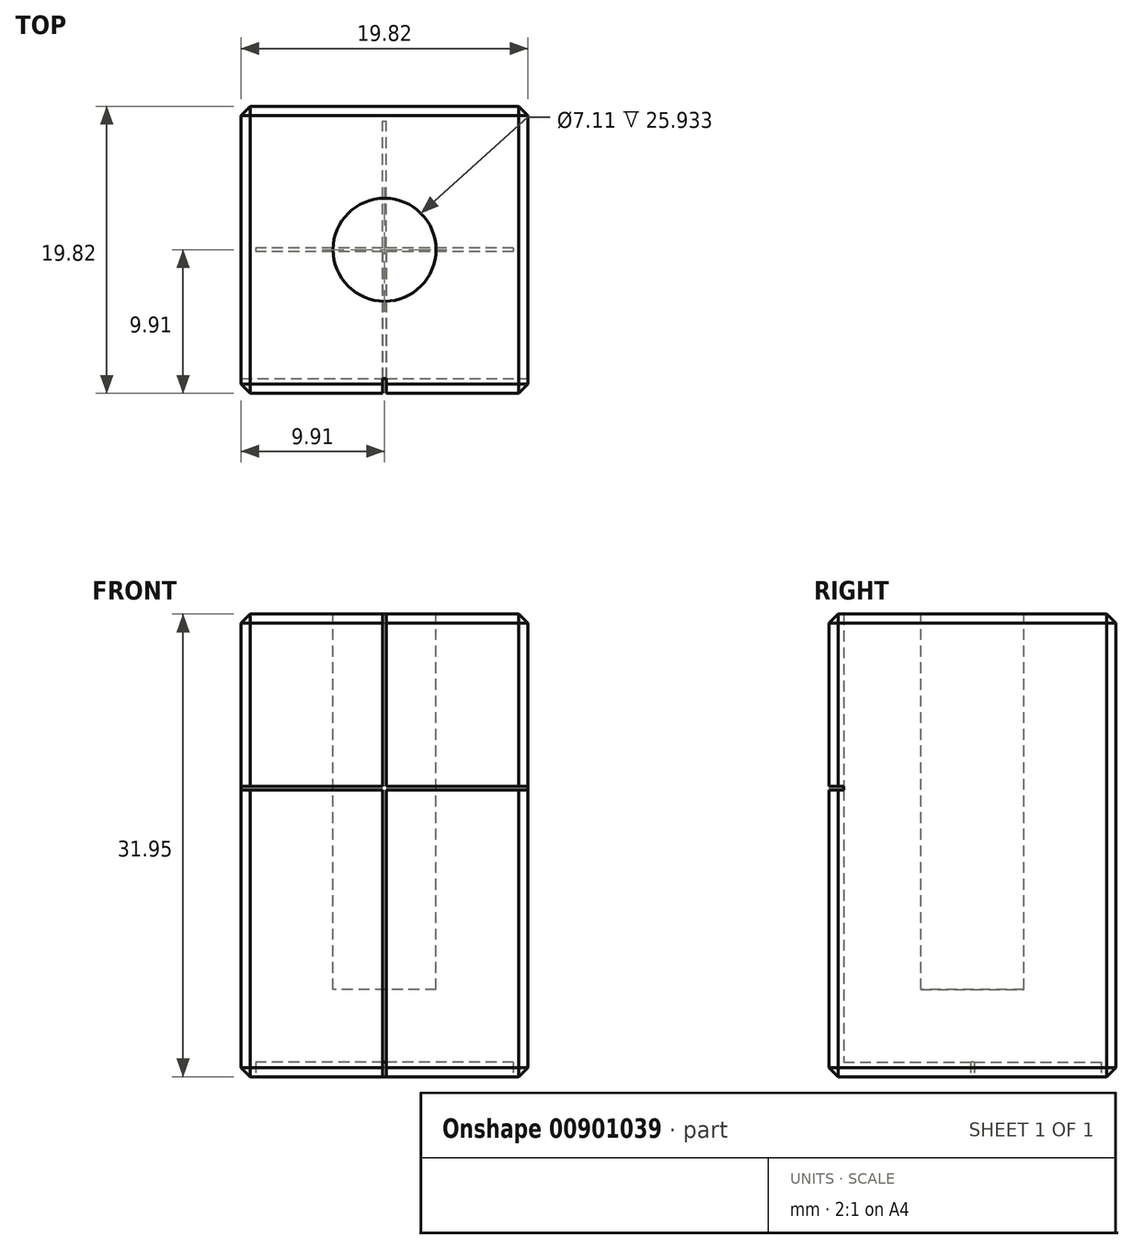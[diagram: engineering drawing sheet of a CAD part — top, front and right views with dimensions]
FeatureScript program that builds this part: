
annotation { "Feature Type Name" : "Feature", "Feature Type Description" : "" }
export const myFeature = defineFeature(function(context is Context, id is Id, definition is map)
    precondition{}
    {
        {
            var Q0;
            Q0=qCreatedBy(makeId("Top.planeOp"),FACE);
            var sketch = newSketch(context, id + "F0", { "sketchPlane" : qUnion([Q0])});
            skLineSegment(sketch, "E0.bottom", {"start": v(9.9, 9.9) * mm, "end": v(-9.9, 9.9) * mm});
            skLineSegment(sketch, "E0.top", {"start": v(9.9, -9.9) * mm, "end": v(-9.9, -9.9) * mm});
            skLineSegment(sketch, "E0.left", {"start": v(9.9, 9.9) * mm, "end": v(9.9, -9.9) * mm});
            skLineSegment(sketch, "E0.right", {"start": v(-9.9, 9.9) * mm, "end": v(-9.9, -9.9) * mm});
            skPoint(sketch, "E0.middle", {"position": v(0, 0) * mm});
            skSolve(sketch);
        }
        {
            var Q0;
            Q0=makeQuery(id+"F0.imprint","IMPRINT",FACE,{"disambiguationData":[TD([[makeQuery(id+"F0.imprint","IMPRINT",EDGE,{"derivedFrom":sQuery(id+"F0.wireOp",EDGE,"E0.bottom")}),1.0]])]});
            extrude(context, id + "F1", {"entities" : qUnion([Q0]), "depth" : 31.95 * mm, "offsetDistance" : 25.4 * mm});
        }
        {
            var Q0;
            Q0=makeQuery(id+"F1.opExtrude","CAP_FACE",FACE,{"disambiguationData":[OSD([sQuery(id+"F0.wireOp",EDGE,"E0.bottom"),sQuery(id+"F0.wireOp",EDGE,"E0.top"),sQuery(id+"F0.wireOp",EDGE,"E0.left"),sQuery(id+"F0.wireOp",EDGE,"E0.right")])],"isStart":false});
            var sketch = newSketch(context, id + "F2", { "sketchPlane" : qUnion([Q0])});
            skCircle(sketch, "E1", {"center": v(0, 0) * mm, "radius": 3.56 * mm});
            skSolve(sketch);
        }
        {
            var Q0;
            Q0 = qSketchRegion(id + "F2", true);
            extrude(context, id + "F3", {"entities" : qUnion([Q0]), "operationType" : NewBodyOperationType.REMOVE, "oppositeDirection" : true, "depth" : 25.93 * mm, "offsetDistance" : 25.4 * mm});
        }
        {
            var Q0;
            Q0=makeQuery(id+"F1.opExtrude","SWEPT_EDGE",EDGE,{"disambiguationData":[OSD([sQuery(id+"F0.wireOp",EDGE,"E0.bottom"),sQuery(id+"F0.wireOp",EDGE,"E0.right")])]});
            var Q1;
            Q1=makeQuery(id+"F1.opExtrude","SWEPT_EDGE",EDGE,{"disambiguationData":[OSD([sQuery(id+"F0.wireOp",EDGE,"E0.top"),sQuery(id+"F0.wireOp",EDGE,"E0.right")])]});
            var Q2;
            Q2=makeQuery(id+"F1.opExtrude","SWEPT_EDGE",EDGE,{"disambiguationData":[OSD([sQuery(id+"F0.wireOp",EDGE,"E0.top"),sQuery(id+"F0.wireOp",EDGE,"E0.left")])]});
            var Q3;
            Q3=makeQuery(id+"F1.opExtrude","SWEPT_EDGE",EDGE,{"disambiguationData":[OSD([sQuery(id+"F0.wireOp",EDGE,"E0.bottom"),sQuery(id+"F0.wireOp",EDGE,"E0.left")])]});
            var Q4;
            Q4=makeQuery(id+"F1.opExtrude","CAP_EDGE",EDGE,{"disambiguationData":[OSD([sQuery(id+"F0.wireOp",EDGE,"E0.left")])],"isStart":false});
            var Q5;
            Q5=makeQuery(id+"F1.opExtrude","CAP_EDGE",EDGE,{"disambiguationData":[OSD([sQuery(id+"F0.wireOp",EDGE,"E0.top")])],"isStart":false});
            var Q6;
            Q6=makeQuery(id+"F1.opExtrude","CAP_EDGE",EDGE,{"disambiguationData":[OSD([sQuery(id+"F0.wireOp",EDGE,"E0.bottom")])],"isStart":false});
            var Q7;
            Q7=makeQuery(id+"F1.opExtrude","CAP_EDGE",EDGE,{"disambiguationData":[OSD([sQuery(id+"F0.wireOp",EDGE,"E0.right")])],"isStart":false});
            var Q8;
            Q8=makeQuery(id+"F1.opExtrude","CAP_EDGE",EDGE,{"disambiguationData":[OSD([sQuery(id+"F0.wireOp",EDGE,"E0.left")])],"isStart":true});
            var Q9;
            Q9=makeQuery(id+"F1.opExtrude","CAP_EDGE",EDGE,{"disambiguationData":[OSD([sQuery(id+"F0.wireOp",EDGE,"E0.bottom")])],"isStart":true});
            var Q10;
            Q10=makeQuery(id+"F1.opExtrude","CAP_EDGE",EDGE,{"disambiguationData":[OSD([sQuery(id+"F0.wireOp",EDGE,"E0.top")])],"isStart":true});
            var Q11;
            Q11=makeQuery(id+"F1.opExtrude","CAP_EDGE",EDGE,{"disambiguationData":[OSD([sQuery(id+"F0.wireOp",EDGE,"E0.right")])],"isStart":true});
            chamfer(context, id + "F4", {"entities" : qUnion([Q0, Q1, Q2, Q3, Q4, Q5, Q6, Q7, Q8, Q9, Q10, Q11]), "width" : 0.64 * mm, "tangentPropagation" : true});
        }
        {
            var Q0;
            Q0=makeQuery(id+"F1.opExtrude","SWEPT_FACE",FACE,{"disambiguationData":[OSD([sQuery(id+"F0.wireOp",EDGE,"E0.top")])]});
            var sketch = newSketch(context, id + "F5", { "sketchPlane" : qUnion([Q0])});
            skLineSegment(sketch, "E2", {"start": v(9.9, 19.94) * mm, "end": v(-9.9, 19.94) * mm, "construction": true});
            skLineSegment(sketch, "E3.bottom", {"start": v(-0.13, 31.95) * mm, "end": v(0.13, 31.95) * mm});
            skLineSegment(sketch, "E3.top", {"start": v(-0.13, 0) * mm, "end": v(0.13, 0) * mm});
            skLineSegment(sketch, "E3.left", {"start": v(-0.13, 31.95) * mm, "end": v(-0.13, 0) * mm});
            skLineSegment(sketch, "E3.right", {"start": v(0.13, 31.95) * mm, "end": v(0.13, 0) * mm});
            skLineSegment(sketch, "E4.bottom", {"start": v(-9.9, 20.07) * mm, "end": v(9.9, 20.07) * mm});
            skLineSegment(sketch, "E4.top", {"start": v(-9.9, 19.81) * mm, "end": v(9.9, 19.81) * mm});
            skLineSegment(sketch, "E4.left", {"start": v(-9.9, 20.07) * mm, "end": v(-9.9, 19.81) * mm});
            skLineSegment(sketch, "E4.right", {"start": v(9.9, 20.07) * mm, "end": v(9.9, 19.81) * mm});
            skSolve(sketch);
        }
        {
            var Q0;
            Q0 = qSketchRegion(id + "F5", true);
            extrude(context, id + "F6", {"entities" : qUnion([Q0]), "operationType" : NewBodyOperationType.REMOVE, "oppositeDirection" : true, "depth" : 1.02 * mm, "offsetDistance" : 25.4 * mm});
        }
        {
            var Q0;
            Q0=makeQuery(id+"F1.opExtrude","CAP_FACE",FACE,{"disambiguationData":[OSD([sQuery(id+"F0.wireOp",EDGE,"E0.bottom"),sQuery(id+"F0.wireOp",EDGE,"E0.top"),sQuery(id+"F0.wireOp",EDGE,"E0.left"),sQuery(id+"F0.wireOp",EDGE,"E0.right")])],"isStart":true});
            var sketch = newSketch(context, id + "F7", { "sketchPlane" : qUnion([Q0])});
            skLineSegment(sketch, "E5.bottom", {"start": v(-0.13, 8.9) * mm, "end": v(0.13, 8.9) * mm});
            skLineSegment(sketch, "E5.top", {"start": v(-0.13, -8.9) * mm, "end": v(0.13, -8.9) * mm});
            skLineSegment(sketch, "E5.left", {"start": v(-0.13, 8.9) * mm, "end": v(-0.13, -8.9) * mm});
            skLineSegment(sketch, "E5.right", {"start": v(0.13, 8.9) * mm, "end": v(0.13, -8.9) * mm});
            skLineSegment(sketch, "E6.bottom", {"start": v(8.9, -0.13) * mm, "end": v(-8.9, -0.13) * mm});
            skLineSegment(sketch, "E6.top", {"start": v(8.9, 0.13) * mm, "end": v(-8.9, 0.13) * mm});
            skLineSegment(sketch, "E6.left", {"start": v(8.9, -0.13) * mm, "end": v(8.9, 0.13) * mm});
            skLineSegment(sketch, "E6.right", {"start": v(-8.9, -0.13) * mm, "end": v(-8.9, 0.13) * mm});
            skSolve(sketch);
        }
        {
            var Q0;
            Q0 = qSketchRegion(id + "F7", true);
            extrude(context, id + "F8", {"entities" : qUnion([Q0]), "operationType" : NewBodyOperationType.REMOVE, "oppositeDirection" : true, "depth" : 1.02 * mm, "offsetDistance" : 25.4 * mm});
        }
    });
